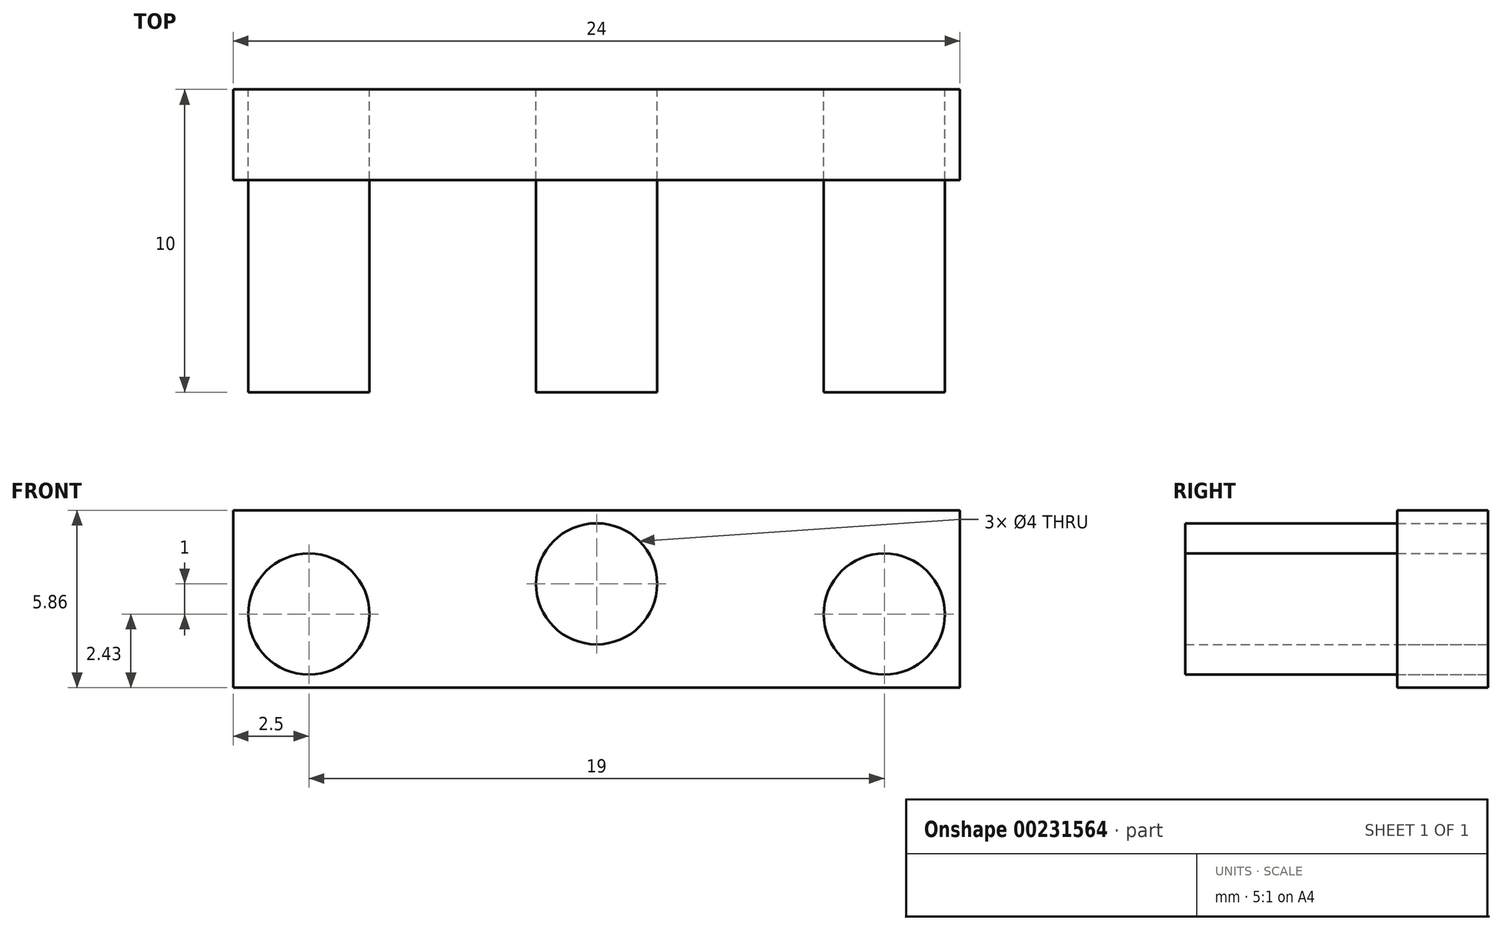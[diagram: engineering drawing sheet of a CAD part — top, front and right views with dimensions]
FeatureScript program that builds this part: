
annotation { "Feature Type Name" : "Feature", "Feature Type Description" : "" }
export const myFeature = defineFeature(function(context is Context, id is Id, definition is map)
    precondition{}
    {
        {
            var Q0;
            Q0=qCreatedBy(makeId("Front.planeOp"),FACE);
            var sketch = newSketch(context, id + "F0", { "sketchPlane" : qUnion([Q0])});
            skCircle(sketch, "E0", {"center": v(0, 1) * mm, "radius": 2 * mm});
            skCircle(sketch, "E1", {"center": v(-9.5, 0) * mm, "radius": 2 * mm});
            skCircle(sketch, "E2", {"center": v(9.5, 0) * mm, "radius": 2 * mm});
            skLineSegment(sketch, "E3.bottom", {"start": v(12, -2.43) * mm, "end": v(-12, -2.43) * mm});
            skLineSegment(sketch, "E3.top", {"start": v(12, 3.43) * mm, "end": v(-12, 3.43) * mm});
            skLineSegment(sketch, "E3.left", {"start": v(12, -2.43) * mm, "end": v(12, 3.43) * mm});
            skLineSegment(sketch, "E3.right", {"start": v(-12, -2.43) * mm, "end": v(-12, 3.43) * mm});
            skSolve(sketch);
        }
        {
            var Q0;
            Q0=makeQuery(id+"F0.imprint","IMPRINT",FACE,{"disambiguationData":[TD([[makeQuery(id+"F0.imprint","IMPRINT",EDGE,{"derivedFrom":sQuery(id+"F0.wireOp",EDGE,"E1")}),1.0]])]});
            var Q1;
            Q1=makeQuery(id+"F0.imprint","IMPRINT",FACE,{"disambiguationData":[TD([[makeQuery(id+"F0.imprint","IMPRINT",EDGE,{"derivedFrom":sQuery(id+"F0.wireOp",EDGE,"E0")}),1.0]])]});
            var Q2;
            Q2=makeQuery(id+"F0.imprint","IMPRINT",FACE,{"disambiguationData":[TD([[makeQuery(id+"F0.imprint","IMPRINT",EDGE,{"derivedFrom":sQuery(id+"F0.wireOp",EDGE,"E2")}),1.0]])]});
            extrude(context, id + "F1", {"entities" : qUnion([Q0, Q1, Q2]), "depth" : 10 * mm});
        }
        {
            var Q0;
            Q0 = qSketchRegion(id + "F0", true);
            extrude(context, id + "F2", {"entities" : qUnion([Q0]), "depth" : 3 * mm});
        }
    });
